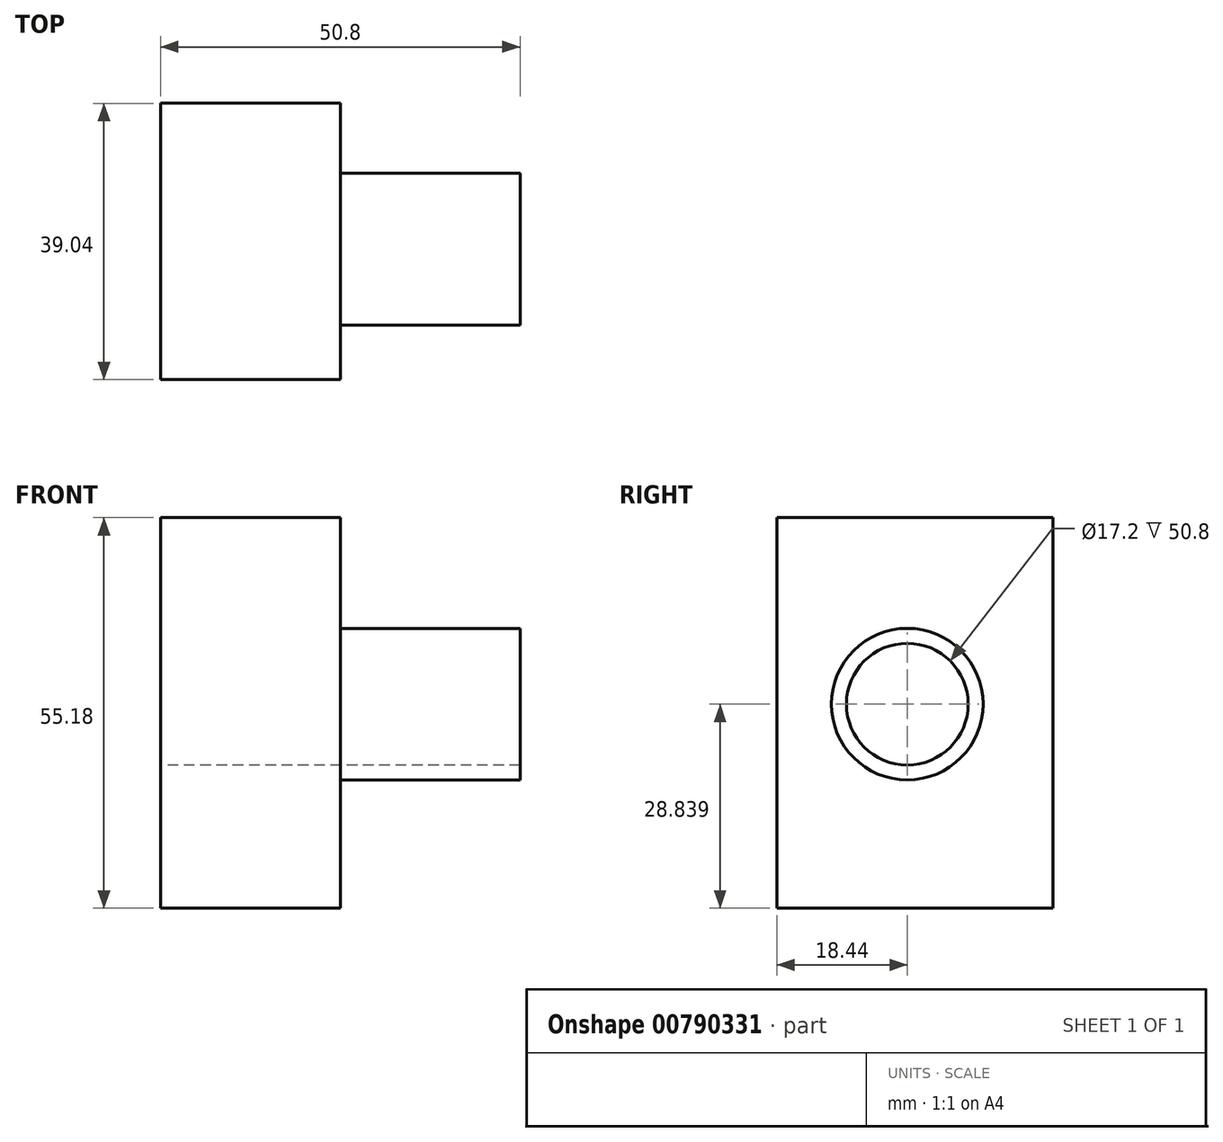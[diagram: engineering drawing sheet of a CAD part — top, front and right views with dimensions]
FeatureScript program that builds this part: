
annotation { "Feature Type Name" : "Feature", "Feature Type Description" : "" }
export const myFeature = defineFeature(function(context is Context, id is Id, definition is map)
    precondition{}
    {
        {
            var Q0;
            Q0=qCreatedBy(makeId("Right.planeOp"),FACE);
            var sketch = newSketch(context, id + "F0", { "sketchPlane" : qUnion([Q0])});
            skLineSegment(sketch, "E0.bottom", {"start": v(-18.44, 37.47) * mm, "end": v(20.6, 37.47) * mm});
            skLineSegment(sketch, "E0.top", {"start": v(-18.44, -17.71) * mm, "end": v(20.6, -17.71) * mm});
            skLineSegment(sketch, "E0.left", {"start": v(-18.44, 37.47) * mm, "end": v(-18.44, -17.71) * mm});
            skLineSegment(sketch, "E0.right", {"start": v(20.6, 37.47) * mm, "end": v(20.6, -17.71) * mm});
            skCircle(sketch, "E1", {"center": v(0, 11.13) * mm, "radius": 10.71 * mm});
            skCircle(sketch, "E2", {"center": v(0, 11.13) * mm, "radius": 8.6 * mm});
            skSolve(sketch);
        }
        {
            var Q0;
            Q0=makeQuery(id+"F0.imprint","IMPRINT",FACE,{"disambiguationData":[TD([[makeQuery(id+"F0.imprint","IMPRINT",EDGE,{"derivedFrom":sQuery(id+"F0.wireOp",EDGE,"E1")}),1.0]])]});
            extrude(context, id + "F1", {"entities" : qUnion([Q0]), "depth" : 50.8 * mm, "offsetDistance" : 25.4 * mm});
        }
        {
            var Q0;
            Q0=makeQuery(id+"F0.imprint","IMPRINT",FACE,{"disambiguationData":[TD([[makeQuery(id+"F0.imprint","IMPRINT",EDGE,{"derivedFrom":sQuery(id+"F0.wireOp",EDGE,"E0.bottom")}),-1.0]])]});
            extrude(context, id + "F2", {"entities" : qUnion([Q0]), "operationType" : NewBodyOperationType.ADD, "depth" : 25.4 * mm, "offsetDistance" : 25.4 * mm});
        }
    });
